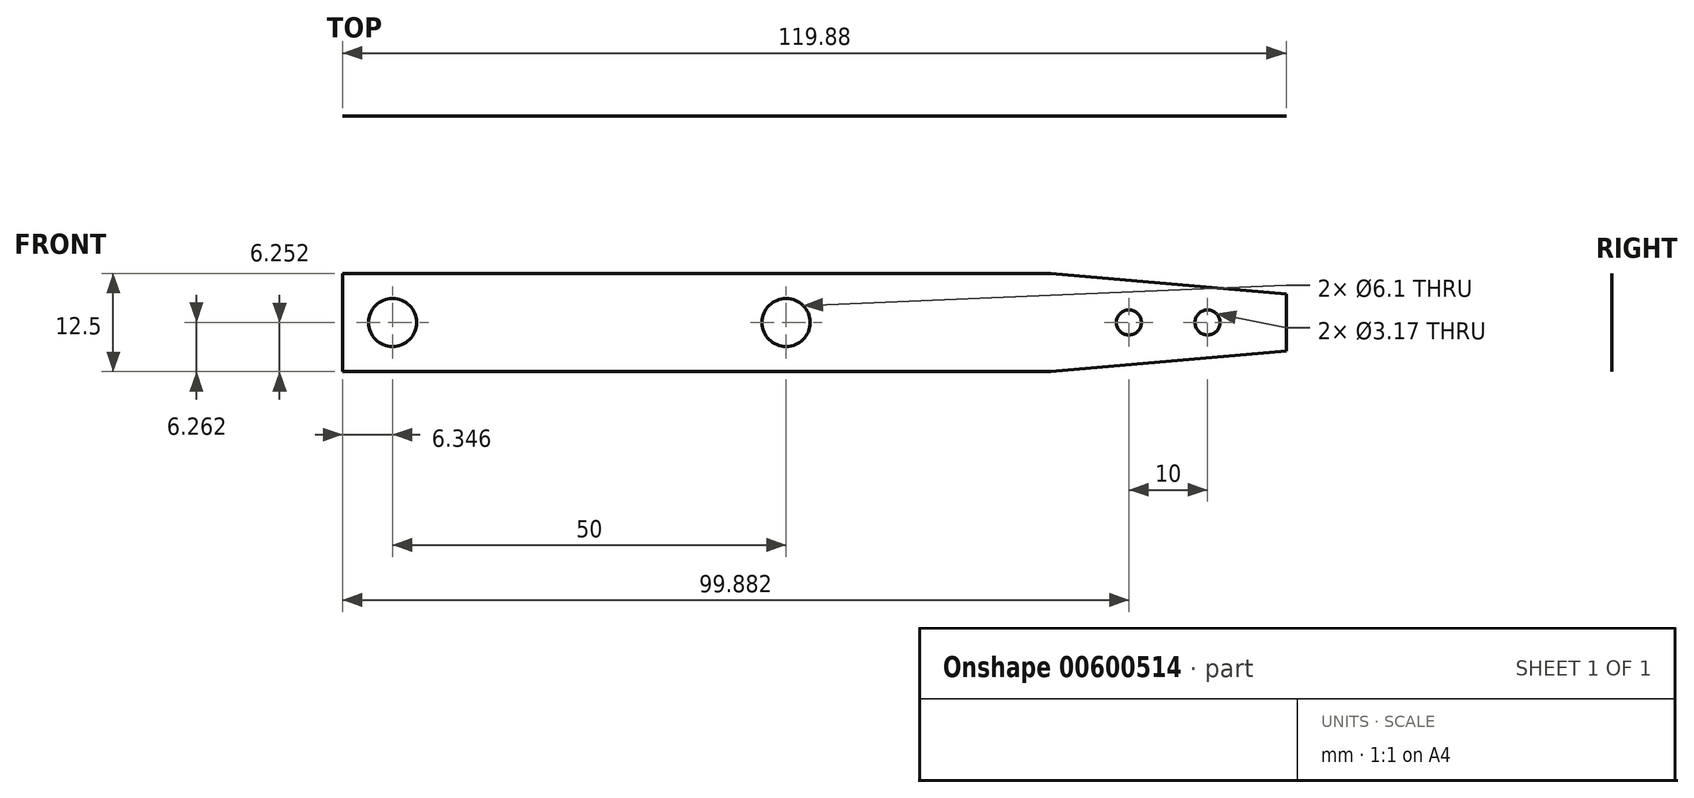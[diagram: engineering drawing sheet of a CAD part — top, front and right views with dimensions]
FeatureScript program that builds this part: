
annotation { "Feature Type Name" : "Feature", "Feature Type Description" : "" }
export const myFeature = defineFeature(function(context is Context, id is Id, definition is map)
    precondition{}
    {
        {
            var Q0;
            Q0=qCreatedBy(makeId("Front.planeOp"),FACE);
            var sketch = newSketch(context, id + "F0", { "sketchPlane" : qUnion([Q0])});
            skLineSegment(sketch, "E0", {"start": v(-36.67, -2.74) * mm, "end": v(53.33, -2.74) * mm});
            skLineSegment(sketch, "E1", {"start": v(-36.67, -15.24) * mm, "end": v(53.33, -15.24) * mm});
            skLineSegment(sketch, "E2", {"start": v(-36.67, -2.74) * mm, "end": v(-36.67, -15.24) * mm});
            skLineSegment(sketch, "E3", {"start": v(53.33, -2.74) * mm, "end": v(83.21, -5.35) * mm});
            skLineSegment(sketch, "E4", {"start": v(53.33, -15.24) * mm, "end": v(83.21, -12.62) * mm});
            skLineSegment(sketch, "E5", {"start": v(83.21, -5.35) * mm, "end": v(83.21, -12.62) * mm});
            skCircle(sketch, "E6", {"center": v(-30.32, -8.99) * mm, "radius": 3.05 * mm});
            skCircle(sketch, "E7", {"center": v(19.68, -8.99) * mm, "radius": 3.05 * mm});
            skCircle(sketch, "E8", {"center": v(73.21, -8.98) * mm, "radius": 1.59 * mm});
            skCircle(sketch, "E9", {"center": v(63.21, -8.98) * mm, "radius": 1.59 * mm});
            skLineSegment(sketch, "E10", {"start": v(73.21, -8.98) * mm, "end": v(83.21, -8.98) * mm});
            skSolve(sketch);
        }
        {
            var Q0;
            Q0 = qSketchRegion(id + "F0", true);
            extrude(context, id + "F1", {"entities" : qUnion([Q0]), "depth" : 1 / 203.2 * mm, "offsetDistance" : 25.4 * mm});
        }
    });
